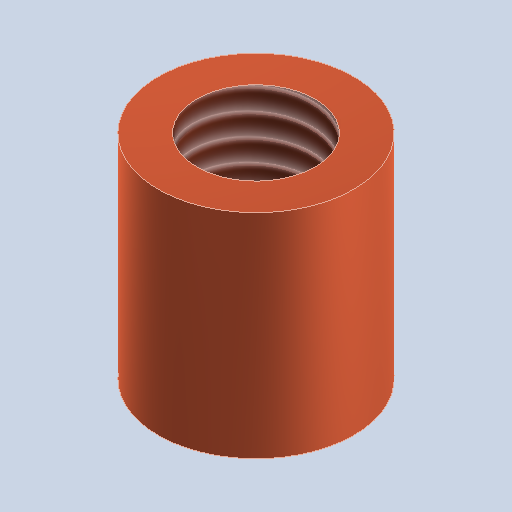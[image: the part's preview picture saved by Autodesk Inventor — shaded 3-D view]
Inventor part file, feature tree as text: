
AUTODESK INVENTOR PART (.ipt)
format: ipt  version: 2025.1 (Build 291241000, 241)  size: 224,768 bytes
history: native  units: mm
features: sketch x2, extrude x1, hole x1
ambient origin geometry x8: Origin, YZ Plane, XZ Plane, XY Plane, X Axis, Y Axis, Z Axis, Center Point
bodies: Solid1 (feature_tree)
feature tree (4):
  extrude  "Extrusion1"  Depth=12.0mm TaperAngle=0.0deg
  hole  "Hole1"  [1 undecoded]
  sketch  "Sketch1"  dims[d0=11.0mm d1=12.0mm d2=0.0mm]
  sketch  "Sketch2"  dims[d3=6.647mm d4=16.0mm d5=4.0mm d6=2.0mm d7=90.0deg d8=22.2mm d9=0.0mm]
note: 1 required parameter value undecoded (feature->parameter linkage not recoverable at this tier; creation-order binding heuristic only, values carry confidence <= 0.55)
